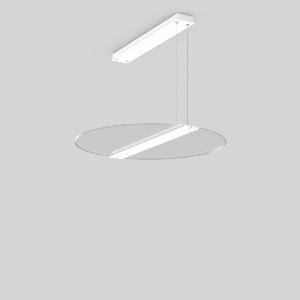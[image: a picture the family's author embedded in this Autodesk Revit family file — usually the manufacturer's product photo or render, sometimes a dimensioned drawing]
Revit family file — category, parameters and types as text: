
# Revit family: twindot_s_round_312353_002_1_a12d
name_source: partatom
category: Lighting Fixtures
units: mm (PartAtom-declared; Revit-internal decimal feet)

## family parameters
Cut with Voids When Loaded = No
Host = Face
Light Source = No
Part Type = Normal
Room Calculation Point = No
Round Connector Dimension = Use Diameter
Shared = No

## types (1)
- TWINDOT S round (1 x LED Modul 840, 4500 lm, 4000)
    Apparent Load = 39 VA
    CIE Flux Codes = 49 78 94 56 100
    Color Rendering = 80
    Color Temperature = 4000
    Default Elevation = 1800 mm
    Description = Series: TWINDOT S round
LED pendant luminaire with extremely flat and frameless appearance. Middle bar made of aluminium extrusion profile, powder-coated. Transparent light guide made of UV-resistant acrylic glass (PMMA) with TWINDOT prismatic. Light control with perfectly glare-free TWINDOT technology for pleasantly gentle light with soft shadows. Even and wide indirect and direct light distribution. Direct 55%, indirect 45% light emission. 4-point steel cable suspension, steplessly adjustable. Converter integrated in the canopy (powder-coated white). Power supply through suspension cable. 
Colour: traffic white, matt (RAL 9016)
Diameter: 645 mm
Height: 20 mm
Suspension length: 500-1200 mm
Lamp: LED
Socket: without socket
Colour temperature: 4000K
Colour rendering index (CRI): 80
System power: 39 W
Rated luminous flux: 4500 lm
Luminous efficiency: 115 lm/W
Control gear: Regulated power supply
Protection class: I
Type of protection: IP 20
    Height = 20 mm  [stored 0.0656168 ft]
    Lamp = 1 x LED Modul 840
    Lamp Light Flux = 4500 lm
    Lamp count = 1
    Length = 645 mm
    Lifetime = 50000 h
    Luminous efficacy = 115 lm/W
    Manufacturer = RZB
    ModVariant = No
    Model = 312353.002.1
    Mounting Place = Ceiling
    Mounting Type = Pendant
    Number of Poles = 1
    OnlyDefault = Yes
    Power Factor = 1
    Product Name = TWINDOT S round
    Product group = Pendant modular luminaires
    ProductGroupID = 906
    Protection Class = Protection class I
    Protection Degree = IP 20
    RLX_Detail_Level = 1
    RLX_Emergency_Light_Flux = 0 lm
    RLX_Emergency_Type = 0
    RLX_Emergency_Type_DB = No
    RlxData = <blob elided: 36085 chars, md5=2814161c>
    Socket = socket
    Standby Power = 0 W
    System Light Flux = 4500 lm
    System Power = 39 W
    Type Comments = Product without accessories
    Type Image = 312353.002.jpg
    URL = http://relux.com
    VarID = ---
    Voltage = 230 V
    Voltage Range = 220-240 V
    Weight = 0.00 kg
    Width = 0 mm  [stored 0 ft]

note: [stored X ft] marks values corroborated as IEEE doubles in the binary element streams (Revit-internal decimal feet)

## geometry (parser evidence)
native form markers: Blend x4, Sweep x10
no freeform markers — native parametric forms only
